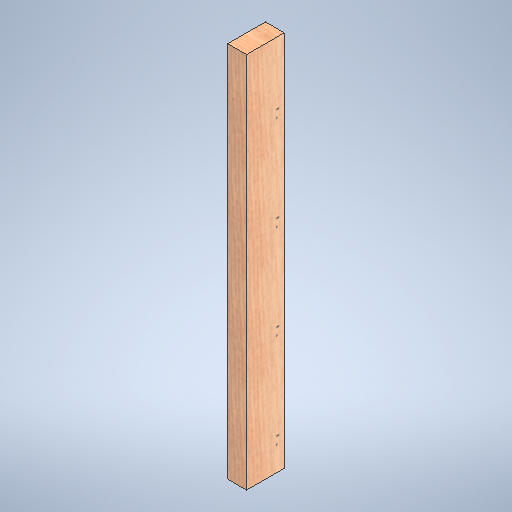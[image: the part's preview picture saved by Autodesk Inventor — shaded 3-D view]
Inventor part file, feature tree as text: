
AUTODESK INVENTOR PART (.ipt)
format: ipt  version: 2025 (Build 290162000, 162)  size: 331,264 bytes
history: native  units: in
note: dims shown in document units (in); Inventor stores cm internally (conversion verified against a paired STEP export)
features: extrude x1, sketch x1
ambient origin geometry x8: Origin, YZ Plane, XZ Plane, XY Plane, X Axis, Y Axis, Z Axis, Center Point
bodies: Solid1 (feature_tree)
feature tree (2):
  extrude  "Extrusion1"  Depth=4.0in
  sketch  "Sketch1"  dims[d0=2.0in d1=4.0in d2=40.0in d3=0.0in]
